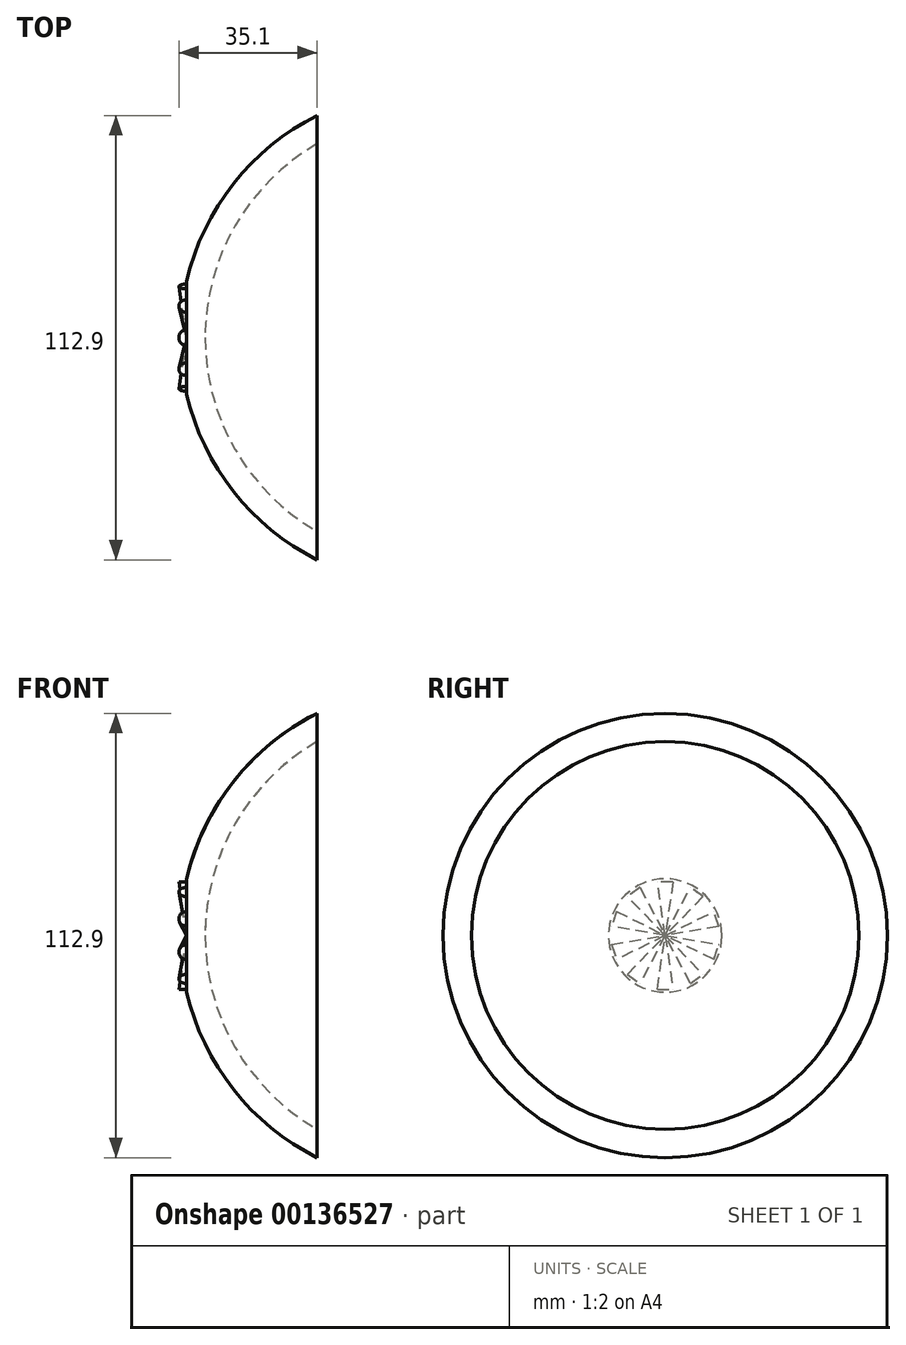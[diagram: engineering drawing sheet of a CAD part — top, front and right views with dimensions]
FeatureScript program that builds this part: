
annotation { "Feature Type Name" : "Feature", "Feature Type Description" : "" }
export const myFeature = defineFeature(function(context is Context, id is Id, definition is map)
    precondition{}
    {
        {
            var Q0;
            Q0=qCreatedBy(makeId("Front.planeOp"),FACE);
            var sketch = newSketch(context, id + "F0", { "sketchPlane" : qUnion([Q0])});
            skArc(sketch, "E0", {"start": v(39.5, 56.45) * mm, "mid": v(14.1, 33.15) * mm, "end": v(4.71, 0) * mm});
            skArc(sketch, "E1.MirrorCS", {"start": v(39.5, -56.45) * mm, "mid": v(14.1, -33.15) * mm, "end": v(4.71, 0) * mm});
            skLineSegment(sketch, "E2", {"start": v(39.5, 56.45) * mm, "end": v(39.5, -56.45) * mm});
            skLineSegment(sketch, "E3", {"start": v(-39.5, 0) * mm, "end": v(39.5, 0) * mm});
            skSolve(sketch);
        }
        {
            var Q0;
            {var subQ0=sQuery(id+"F0.wireOp",EDGE,"8f6d09b5-3b41-475d-8da4-104243e637410.MirrorCS");Q0=makeQuery(id+"F0.imprint","IMPRINT",FACE,{"disambiguationData":[TD([[makeQuery(id+"F0.imprint","IMPRINT",EDGE,{"derivedFrom":subQ0}),-1.0]])]});}
            var Q1;
            {var subQ0=sQuery(id+"F0.wireOp",EDGE,"E0");Q1=makeQuery(id+"F0.imprint","IMPRINT",FACE,{"disambiguationData":[TD([[makeQuery(id+"F0.imprint","IMPRINT",EDGE,{"derivedFrom":subQ0}),1.0]])]});}
            var Q2;
            Q2=sQuery(id+"F0.wireOp",EDGE,"E3");
            revolve(context, id + "F1", {"entities" : qUnion([Q0, Q1]), "axis" : qUnion([Q2]), "revolveType" : RevolveType.FULL});
        }
        {
            var Q0;
            Q0=makeQuery(id+"F1.opRevolve","SWEPT_FACE",FACE,{"disambiguationData":[OSD([sQuery(id+"F0.wireOp",EDGE,"E2")])]});
            shell(context, id + "F2", {"entities" : qUnion([Q0]), "thickness" : 6.35 * mm});
        }
        {
            var Q0;
            Q0=qCreatedBy(makeId("Front.planeOp"),FACE);
            var sketch = newSketch(context, id + "F3", { "sketchPlane" : qUnion([Q0])});
            skPoint(sketch, "E4.middle", {"position": v(0, 0) * mm});
            skLineSegment(sketch, "E5.bottom", {"start": v(6.38, 16) * mm, "end": v(-6.38, 16) * mm});
            skLineSegment(sketch, "E5.top", {"start": v(6.38, -16) * mm, "end": v(-6.38, -16) * mm});
            skLineSegment(sketch, "E5.left", {"start": v(6.38, 16) * mm, "end": v(6.38, -16) * mm});
            skLineSegment(sketch, "E5.right", {"start": v(-6.38, 16) * mm, "end": v(-6.38, -16) * mm});
            skLineSegment(sketch, "E6", {"start": v(-6.38, 0) * mm, "end": v(6.38, 0) * mm});
            skSolve(sketch);
        }
        {
            var Q0;
            {var subQ0=sQuery(id+"F3.wireOp",EDGE,"E5.bottom");Q0=makeQuery(id+"F3.imprint","IMPRINT",FACE,{"disambiguationData":[TD([[makeQuery(id+"F3.imprint","IMPRINT",EDGE,{"derivedFrom":subQ0}),1.0]])]});}
            var Q1;
            Q1=sQuery(id+"F3.wireOp",EDGE,"E6");
            revolve(context, id + "F4", {"operationType" : NewBodyOperationType.REMOVE, "entities" : qUnion([Q0]), "axis" : qUnion([Q1]), "revolveType" : RevolveType.FULL, "oppositeDirection" : true});
        }
        {
            var Q0;
            Q0=makeQuery(id+"F4.boolean.opBoolean","COPY",FACE,{"derivedFrom":makeQuery(id+"F4.opRevolve","SWEPT_FACE",FACE,{"disambiguationData":[OSD([sQuery(id+"F3.wireOp",EDGE,"E5.left")])]})});
            var sketch = newSketch(context, id + "F5", { "sketchPlane" : qUnion([Q0])});
            skLineSegment(sketch, "E7", {"start": v(0, 0) * mm, "end": v(1.99, 13.66) * mm});
            skLineSegment(sketch, "E8", {"start": v(1.99, 13.66) * mm, "end": v(0, 13.66) * mm});
            skLineSegment(sketch, "E9.MirrorCS", {"start": v(0, 0) * mm, "end": v(-1.99, 13.66) * mm});
            skLineSegment(sketch, "E10.MirrorCS", {"start": v(-1.99, 13.66) * mm, "end": v(0, 13.66) * mm});
            skPoint(sketch, "E11.center", {"position": v(0, 0) * mm});
            skLineSegment(sketch, "E12", {"start": v(0, 13.66) * mm, "end": v(0, 0) * mm});
            skLineSegment(sketch, "E13.1.0", {"start": v(0, 0) * mm, "end": v(-6.42, 12.22) * mm});
            skLineSegment(sketch, "E13.1.1", {"start": v(-6.42, 12.22) * mm, "end": v(-8.03, 11.05) * mm});
            skLineSegment(sketch, "E13.1.2", {"start": v(0, 0) * mm, "end": v(-9.64, 9.89) * mm});
            skLineSegment(sketch, "E13.1.3", {"start": v(-9.64, 9.89) * mm, "end": v(-8.03, 11.05) * mm});
            skLineSegment(sketch, "E13.1.4", {"start": v(-8.03, 11.05) * mm, "end": v(0, 0) * mm});
            skLineSegment(sketch, "E13.2.0", {"start": v(0, 0) * mm, "end": v(-12.38, 6.11) * mm});
            skLineSegment(sketch, "E13.2.1", {"start": v(-12.38, 6.11) * mm, "end": v(-13, 4.22) * mm});
            skLineSegment(sketch, "E13.2.2", {"start": v(0, 0) * mm, "end": v(-13.6, 2.33) * mm});
            skLineSegment(sketch, "E13.2.3", {"start": v(-13.6, 2.33) * mm, "end": v(-13, 4.22) * mm});
            skLineSegment(sketch, "E13.2.4", {"start": v(-13, 4.22) * mm, "end": v(0, 0) * mm});
            skLineSegment(sketch, "E13.3.0", {"start": v(0, 0) * mm, "end": v(-13.6, -2.33) * mm});
            skLineSegment(sketch, "E13.3.1", {"start": v(-13.6, -2.33) * mm, "end": v(-13, -4.22) * mm});
            skLineSegment(sketch, "E13.3.2", {"start": v(0, 0) * mm, "end": v(-12.38, -6.11) * mm});
            skLineSegment(sketch, "E13.3.3", {"start": v(-12.38, -6.11) * mm, "end": v(-13, -4.22) * mm});
            skLineSegment(sketch, "E13.3.4", {"start": v(-13, -4.22) * mm, "end": v(0, 0) * mm});
            skLineSegment(sketch, "E13.4.0", {"start": v(0, 0) * mm, "end": v(-9.64, -9.89) * mm});
            skLineSegment(sketch, "E13.4.1", {"start": v(-9.64, -9.89) * mm, "end": v(-8.03, -11.05) * mm});
            skLineSegment(sketch, "E13.4.2", {"start": v(0, 0) * mm, "end": v(-6.42, -12.22) * mm});
            skLineSegment(sketch, "E13.4.3", {"start": v(-6.42, -12.22) * mm, "end": v(-8.03, -11.05) * mm});
            skLineSegment(sketch, "E13.4.4", {"start": v(-8.03, -11.05) * mm, "end": v(0, 0) * mm});
            skLineSegment(sketch, "E13.5.0", {"start": v(0, 0) * mm, "end": v(-1.99, -13.66) * mm});
            skLineSegment(sketch, "E13.5.1", {"start": v(-1.99, -13.66) * mm, "end": v(0, -13.66) * mm});
            skLineSegment(sketch, "E13.5.2", {"start": v(0, 0) * mm, "end": v(1.99, -13.66) * mm});
            skLineSegment(sketch, "E13.5.3", {"start": v(1.99, -13.66) * mm, "end": v(0, -13.66) * mm});
            skLineSegment(sketch, "E13.5.4", {"start": v(0, -13.66) * mm, "end": v(0, 0) * mm});
            skLineSegment(sketch, "E13.6.0", {"start": v(0, 0) * mm, "end": v(6.42, -12.22) * mm});
            skLineSegment(sketch, "E13.6.1", {"start": v(6.42, -12.22) * mm, "end": v(8.03, -11.05) * mm});
            skLineSegment(sketch, "E13.6.2", {"start": v(0, 0) * mm, "end": v(9.64, -9.89) * mm});
            skLineSegment(sketch, "E13.6.3", {"start": v(9.64, -9.89) * mm, "end": v(8.03, -11.05) * mm});
            skLineSegment(sketch, "E13.6.4", {"start": v(8.03, -11.05) * mm, "end": v(0, 0) * mm});
            skLineSegment(sketch, "E13.7.0", {"start": v(0, 0) * mm, "end": v(12.38, -6.11) * mm});
            skLineSegment(sketch, "E13.7.1", {"start": v(12.38, -6.11) * mm, "end": v(13, -4.22) * mm});
            skLineSegment(sketch, "E13.7.2", {"start": v(0, 0) * mm, "end": v(13.6, -2.33) * mm});
            skLineSegment(sketch, "E13.7.3", {"start": v(13.6, -2.33) * mm, "end": v(13, -4.22) * mm});
            skLineSegment(sketch, "E13.7.4", {"start": v(13, -4.22) * mm, "end": v(0, 0) * mm});
            skLineSegment(sketch, "E13.8.0", {"start": v(0, 0) * mm, "end": v(13.6, 2.33) * mm});
            skLineSegment(sketch, "E13.8.1", {"start": v(13.6, 2.33) * mm, "end": v(13, 4.22) * mm});
            skLineSegment(sketch, "E13.8.2", {"start": v(0, 0) * mm, "end": v(12.38, 6.11) * mm});
            skLineSegment(sketch, "E13.8.3", {"start": v(12.38, 6.11) * mm, "end": v(13, 4.22) * mm});
            skLineSegment(sketch, "E13.8.4", {"start": v(13, 4.22) * mm, "end": v(0, 0) * mm});
            skLineSegment(sketch, "E13.9.0", {"start": v(0, 0) * mm, "end": v(9.64, 9.89) * mm});
            skLineSegment(sketch, "E13.9.1", {"start": v(9.64, 9.89) * mm, "end": v(8.03, 11.05) * mm});
            skLineSegment(sketch, "E13.9.2", {"start": v(0, 0) * mm, "end": v(6.42, 12.22) * mm});
            skLineSegment(sketch, "E13.9.3", {"start": v(6.42, 12.22) * mm, "end": v(8.03, 11.05) * mm});
            skLineSegment(sketch, "E13.9.4", {"start": v(8.03, 11.05) * mm, "end": v(0, 0) * mm});
            skSolve(sketch);
        }
        {
            var Q0;
            Q0=makeQuery(id+"F5.imprint","IMPRINT",FACE,{"disambiguationData":[TD([[makeQuery(id+"F5.imprint","IMPRINT",EDGE,{"derivedFrom":sQuery(id+"F5.wireOp",EDGE,"E9.MirrorCS")}),-1.0]])]});
            var Q1;
            Q1=sQuery(id+"F5.wireOp",EDGE,"E12");
            revolve(context, id + "F6", {"operationType" : NewBodyOperationType.ADD, "entities" : qUnion([Q0]), "axis" : qUnion([Q1]), "revolveType" : RevolveType.FULL});
        }
        {
            var Q0;
            Q0=makeQuery(id+"F5.imprint","IMPRINT",FACE,{"disambiguationData":[TD([[makeQuery(id+"F5.imprint","IMPRINT",EDGE,{"derivedFrom":sQuery(id+"F5.wireOp",EDGE,"E13.1.0")}),1.0]])]});
            var Q1;
            Q1=sQuery(id+"F5.wireOp",EDGE,"E13.1.4");
            revolve(context, id + "F7", {"operationType" : NewBodyOperationType.ADD, "entities" : qUnion([Q0]), "axis" : qUnion([Q1]), "revolveType" : RevolveType.FULL});
        }
        {
            var Q0;
            Q0=makeQuery(id+"F5.imprint","IMPRINT",FACE,{"disambiguationData":[TD([[makeQuery(id+"F5.imprint","IMPRINT",EDGE,{"derivedFrom":sQuery(id+"F5.wireOp",EDGE,"E13.2.0")}),1.0]])]});
            var Q1;
            Q1=sQuery(id+"F5.wireOp",EDGE,"E13.2.4");
            revolve(context, id + "F8", {"operationType" : NewBodyOperationType.ADD, "entities" : qUnion([Q0]), "axis" : qUnion([Q1]), "revolveType" : RevolveType.FULL});
        }
        {
            var Q0;
            Q0=makeQuery(id+"F5.imprint","IMPRINT",FACE,{"disambiguationData":[TD([[makeQuery(id+"F5.imprint","IMPRINT",EDGE,{"derivedFrom":sQuery(id+"F5.wireOp",EDGE,"E13.3.0")}),1.0]])]});
            var Q1;
            Q1=sQuery(id+"F5.wireOp",EDGE,"E13.3.4");
            revolve(context, id + "F9", {"operationType" : NewBodyOperationType.ADD, "entities" : qUnion([Q0]), "axis" : qUnion([Q1]), "revolveType" : RevolveType.FULL});
        }
        {
            var Q0;
            Q0=makeQuery(id+"F5.imprint","IMPRINT",FACE,{"disambiguationData":[TD([[makeQuery(id+"F5.imprint","IMPRINT",EDGE,{"derivedFrom":sQuery(id+"F5.wireOp",EDGE,"E13.4.0")}),1.0]])]});
            var Q1;
            Q1=sQuery(id+"F5.wireOp",EDGE,"E13.4.4");
            revolve(context, id + "F10", {"operationType" : NewBodyOperationType.ADD, "entities" : qUnion([Q0]), "axis" : qUnion([Q1]), "revolveType" : RevolveType.FULL});
        }
        {
            var Q0;
            Q0=makeQuery(id+"F5.imprint","IMPRINT",FACE,{"disambiguationData":[TD([[makeQuery(id+"F5.imprint","IMPRINT",EDGE,{"derivedFrom":sQuery(id+"F5.wireOp",EDGE,"E13.5.0")}),1.0]])]});
            var Q1;
            Q1=sQuery(id+"F5.wireOp",EDGE,"E13.5.4");
            revolve(context, id + "F11", {"operationType" : NewBodyOperationType.ADD, "entities" : qUnion([Q0]), "axis" : qUnion([Q1]), "revolveType" : RevolveType.FULL});
        }
        {
            var Q0;
            Q0=makeQuery(id+"F5.imprint","IMPRINT",FACE,{"disambiguationData":[TD([[makeQuery(id+"F5.imprint","IMPRINT",EDGE,{"derivedFrom":sQuery(id+"F5.wireOp",EDGE,"E13.9.2")}),-1.0]])]});
            var Q1;
            Q1=sQuery(id+"F5.wireOp",EDGE,"E13.9.4");
            revolve(context, id + "F12", {"operationType" : NewBodyOperationType.ADD, "entities" : qUnion([Q0]), "axis" : qUnion([Q1]), "revolveType" : RevolveType.FULL});
        }
        {
            var Q0;
            Q0=makeQuery(id+"F5.imprint","IMPRINT",FACE,{"disambiguationData":[TD([[makeQuery(id+"F5.imprint","IMPRINT",EDGE,{"derivedFrom":sQuery(id+"F5.wireOp",EDGE,"E13.8.2")}),-1.0]])]});
            var Q1;
            Q1=sQuery(id+"F5.wireOp",EDGE,"E13.8.4");
            revolve(context, id + "F13", {"operationType" : NewBodyOperationType.ADD, "entities" : qUnion([Q0]), "axis" : qUnion([Q1]), "revolveType" : RevolveType.FULL});
        }
        {
            var Q0;
            Q0=makeQuery(id+"F5.imprint","IMPRINT",FACE,{"disambiguationData":[TD([[makeQuery(id+"F5.imprint","IMPRINT",EDGE,{"derivedFrom":sQuery(id+"F5.wireOp",EDGE,"E13.7.2")}),-1.0]])]});
            var Q1;
            Q1=sQuery(id+"F5.wireOp",EDGE,"E13.7.4");
            revolve(context, id + "F14", {"operationType" : NewBodyOperationType.ADD, "entities" : qUnion([Q0]), "axis" : qUnion([Q1]), "revolveType" : RevolveType.FULL});
        }
        {
            var Q0;
            Q0=makeQuery(id+"F5.imprint","IMPRINT",FACE,{"disambiguationData":[TD([[makeQuery(id+"F5.imprint","IMPRINT",EDGE,{"derivedFrom":sQuery(id+"F5.wireOp",EDGE,"E13.6.2")}),-1.0]])]});
            var Q1;
            Q1=sQuery(id+"F5.wireOp",EDGE,"E13.6.4");
            revolve(context, id + "F15", {"operationType" : NewBodyOperationType.ADD, "entities" : qUnion([Q0]), "axis" : qUnion([Q1]), "revolveType" : RevolveType.FULL});
        }
    });
